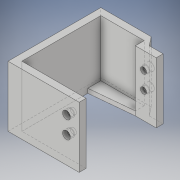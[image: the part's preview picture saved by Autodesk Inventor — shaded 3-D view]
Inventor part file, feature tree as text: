
AUTODESK INVENTOR PART (.ipt)
format: ipt  version: 2019 (Build 230136000, 136)  size: 147,456 bytes
history: native  units: mm
features: sketch x4, extrude x2, hole x2
ambient origin geometry x8: Origin, YZ Plane, XZ Plane, XY Plane, X Axis, Y Axis, Z Axis, Center Point
bodies: Body1 (feature_tree)
feature tree (8):
  extrude  "Extrusion10"  Depth=25.0mm
  extrude  "Extrusion12"  Depth=12.0mm
  hole  "Hole4"  [1 undecoded]
  hole  "Hole5"  [1 undecoded]
  sketch  "Sketch14"  dims[d59=45.5mm d60=25.0mm]
  sketch  "Sketch17"  dims[d61=5.1mm d62=12.0mm]
  sketch  "Sketch18"  dims[d64=4.0mm d65=4.0mm]
  sketch  "Sketch19"  dims[d66=4.0mm d67=4.0mm d68=8.0mm d69=35.0mm d70=0.0mm d75=2.5mm d76=0.0mm d77=29.7mm d78=20.0mm d79=3.5mm d80=6.0mm d81=4.5mm d82=7.6mm d83=90.0deg d84=6.5mm d85=0.0mm d86=3.5mm d87=6.0mm d88=4.5mm d89=2.5mm d90=90.0deg d91=6.5mm d92=0.0mm]
note: 2 required parameter values undecoded (feature->parameter linkage not recoverable at this tier; creation-order binding heuristic only, values carry confidence <= 0.55)
